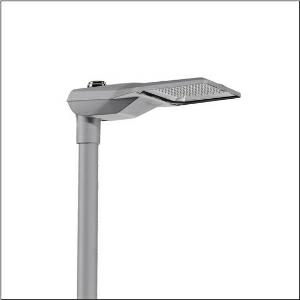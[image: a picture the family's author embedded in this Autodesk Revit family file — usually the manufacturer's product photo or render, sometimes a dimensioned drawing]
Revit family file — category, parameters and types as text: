
# Revit family: streetlight_sl_21_midi___p1_0a_5xe7a47n08lb_4b2d
name_source: partatom
category: Lighting Fixtures
units: mm (PartAtom-declared; Revit-internal decimal feet)

## family parameters
Cut with Voids When Loaded = No
Host = Face
Light Source = No
Part Type = Normal
Room Calculation Point = No
Round Connector Dimension = Use Diameter
Shared = No

## types (1)
- --- (1 x LED, 14950 lm, 98.3 W, 4000K)
    Apparent Load = 98 VA
    CIE Flux Codes = 21 50 90 100 100
    Color Rendering = 70
    Color Temperature = 4000K
    Default Elevation = 1800 mm
    Description = Streetlight SL 21 midi, mast luminaire, primary light control with lens, of PMMA, primary optical cover: cover, of toughened safety glass, transparent, light distribution: P1.0a, light emission: direct distribution, primary light characteristic: asymmetric, installation type: side-entry, LED, 3G 2.5mm², High Power LED, rated luminous flux: 14.950lm, luminous efficacy: 152lm/W, light colour: 740, colour temperature: 4000K, control gear: NEMA (7pin), control: overheat protection, pre-setting: linear dimming characteristic, constant luminous flux control, time-dependent luminous flux control, flexible luminous flux parameterisation, mains connection: 220..240V, AC, 50/60Hz, connection cable pre-assembled, cable length: 10,5m, wiring characteristics: H05VV-F, start of lifetime: 98W, end of service life: 101W, reduction: 45W, luminaire housing, of diecast aluminium (EN AC-44300), powder-coated, SITECO metallic grey (DB 702S), corrosivity category C5 high according to DIN EN ISO 12944, multi-level sealing system, sealing non-destructively replaceable, inclination adjustable: 0°, 5°, 10°, 15°, length: 644mm, width: 335mm, height: 110mm, spigot size: 42mm (side-entry), mounting height: 4..8m, protection rating (complete): IP66, insulation class (complete): insulation class I (protective earthing), certification: CE, ENEC, ENEC+, VDE, impact resistance: IK10, permissible operating ambient temperature for outdoor applications: -40..+50°C, standard-compliant lighting for roads and squares, packaging unit: 1 piece

Light Distribution: P1.0a
    Height = 111 mm
    Lamp = 1 x LED
    Lamp Light Flux = 14950 lm
    Lamp Power = 98.3 W
    Lamp count = 1
    Length = 644 mm
    Luminous efficacy = 152 lm/W
    Manufacturer = Siteco
    ModVariant = No
    Model = 5XE7A47N08LB
    Number of Poles = 1
    OnlyDefault = Yes
    Power Factor = 1
    Product Name = Streetlight SL 21 midi | P1.0a
    Product group = mast luminaire | pylon top
    ProductGroupID = 6100
    Protection Class = Protection class I
    Protection Degree = IP 66
    RLX_Detail_Level = 1
    RLX_Emergency_Light_Flux = 0 lm
    RLX_Emergency_Type = 0
    RLX_Emergency_Type_DB = No
    RlxData = <blob elided: 37961 chars, md5=c5619735>
    Socket = socket
    Standby Power = 0 W
    System Light Flux = 14950 lm
    System Power = 98 W
    Type Comments = factory setting: luminous flux: 100 % | dim-lin: 254 | 1020 mA
    Type Image = l_1294377.jpg
    URL = http://relux.com
    VarID = @adj_133977
    Voltage = 0 V
    Weight = 0.00 kg
    Width = 336 mm

## geometry (parser evidence)
native form markers: Blend x4, Sweep x11
no freeform markers — native parametric forms only
